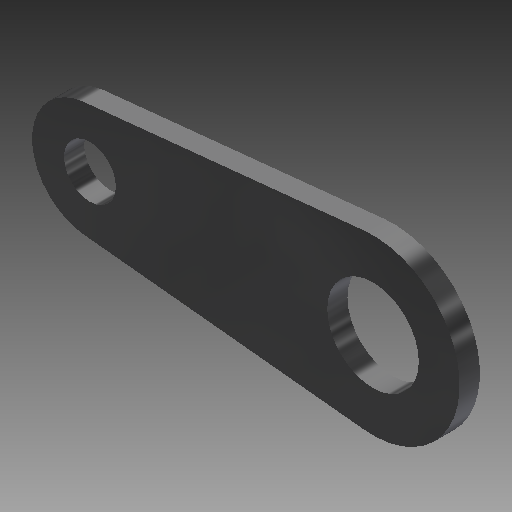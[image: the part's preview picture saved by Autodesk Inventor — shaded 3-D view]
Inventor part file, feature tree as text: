
AUTODESK INVENTOR PART (.ipt)
format: ipt  version: 2019 (Build 230136000, 136)  size: 113,152 bytes
history: native  units: mm
features: sketch x3, hole x2, extrude x1
ambient origin geometry x8: Origin, YZ Plane, XZ Plane, XY Plane, X Axis, Y Axis, Z Axis, Center Point
bodies: Solid1 (feature_tree)
feature tree (6):
  extrude  "Extrusion1"  Depth=30.0mm
  hole  "Hole1"  [1 undecoded]
  hole  "Hole2"  [1 undecoded]
  sketch  "Sketch1"  dims[d0=20.0mm d1=30.0mm]
  sketch  "Sketch2"  dims[d2=49.0mm d3=3.5mm d4=0.0mm]
  sketch  "Sketch3"  dims[d5=15.84mm d6=6.0mm d7=4.0mm d8=2.0mm d9=90.0deg d10=8.0mm d11=20.594885mm d12=9.0mm d13=6.0mm d14=4.0mm d15=2.0mm d16=90.0deg d17=8.0mm d18=20.594885mm]
note: 2 required parameter values undecoded (feature->parameter linkage not recoverable at this tier; creation-order binding heuristic only, values carry confidence <= 0.55)
